# Revit family: Planter Top
name_source: partatom
category: Furniture
revit_build: Autodesk Revit 2018 (Build: 20181011_1500(x64)
units: mm (PartAtom-declared; Revit-internal decimal feet)

## family parameters
Always vertical = Yes
Cut with Voids When Loaded = No
OmniClass Number = 23.40.20.00
OmniClass Title = General Furniture and Specialties
Room Calculation Point = No
Shared = No
Work Plane-Based = No

## types (2) — shared parameters
Carcass_Material = Steel, Mild
Classification.Uniclass.Pr.Description = Steel Plant Containers
Classification.Uniclass.Pr.Number = PR_45_63_84
Colour = Vision Colour Palette
Depth = 470 mm  [stored 1.54199 ft]
Expected Life = >10 years
Height = 152 mm  [stored 0.498688 ft]
Manufacturer = Bisley
Product Information = Lateralfile Planter Top
Range = LateralFile
Revision = V1
Routine Maintenance = We recommend you clean your unit with warm water and a mild detergent solution. A damp cloth can be used to remove dust particles.
Uniclass2015Version = V1.3
Warranty = 10 Years
wall thickness = 2 mm  [stored 0.00656168 ft]

## per-type parameters (varying)
| type | Dimensions | Insert Type | Width |
| RP08M | 800mm x 152mm x 470mm | Plastic Liner : 800 planter | 800 mm  [stored 2.62467 ft] |
| RP10M | 1000mm x 152mm x 470mm | Plastic Liner : 1000 planter | 1000 mm  [stored 3.28084 ft] |

note: column(s) folded — value = type name in every type: Model

note: [stored X ft] marks values corroborated as IEEE doubles in the binary element streams (Revit-internal decimal feet)

## geometry (parser evidence)
native form markers: Sweep x3
no freeform markers — native parametric forms only
